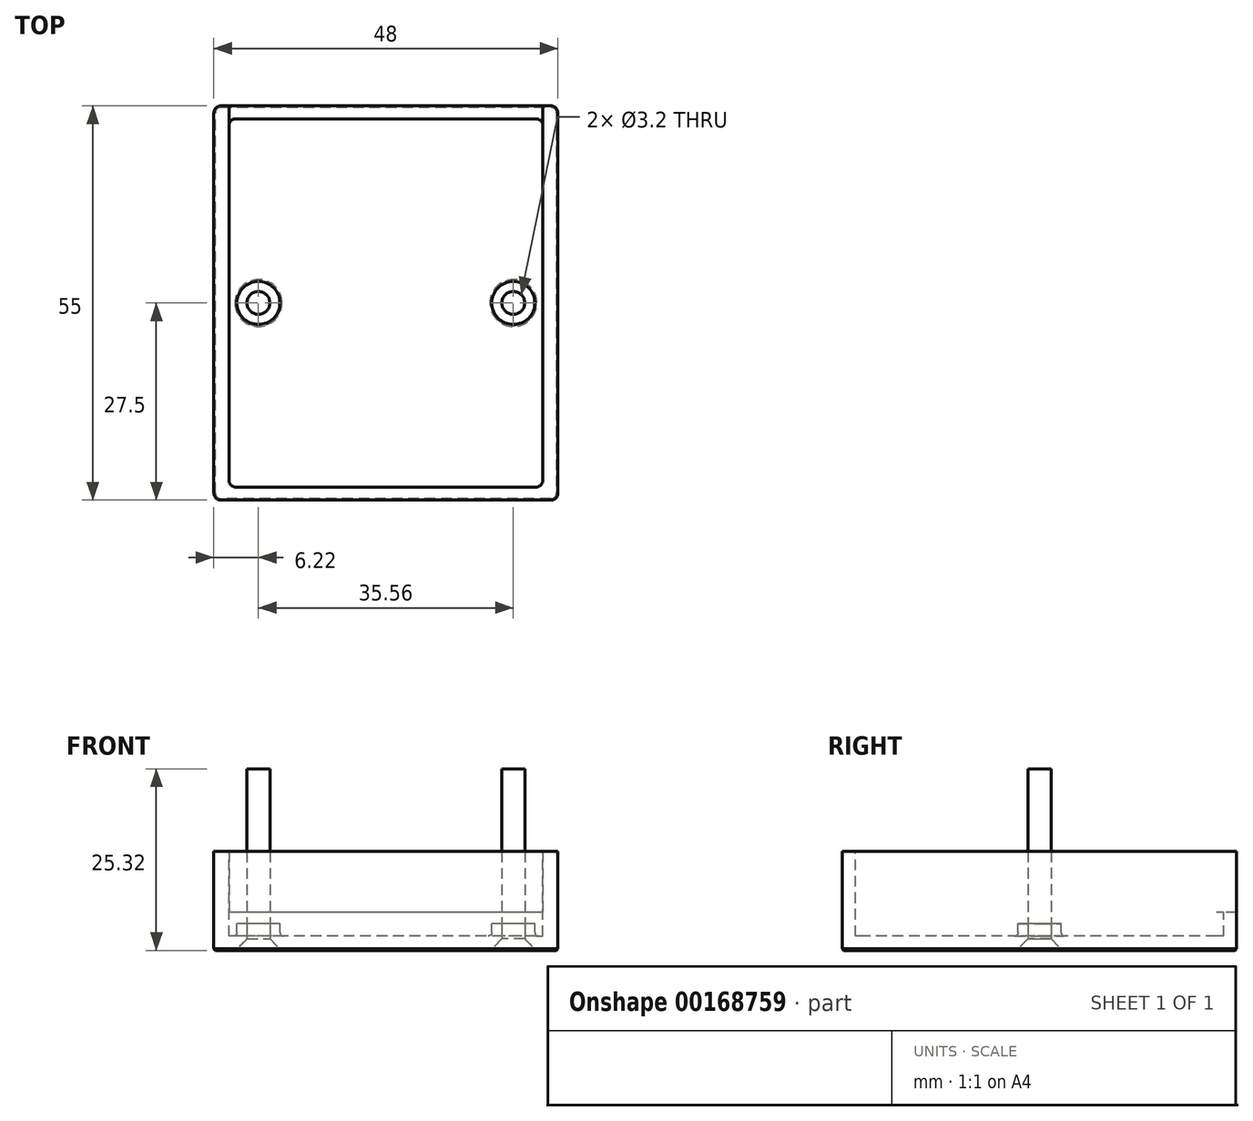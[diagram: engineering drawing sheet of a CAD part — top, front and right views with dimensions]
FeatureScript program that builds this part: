
annotation { "Feature Type Name" : "Feature", "Feature Type Description" : "" }
export const myFeature = defineFeature(function(context is Context, id is Id, definition is map)
    precondition{}
    {
        {
            var Q0;
            Q0=qCreatedBy(makeId("Top.planeOp"),FACE);
            var sketch = newSketch(context, id + "F0", { "sketchPlane" : qUnion([Q0])});
            skLineSegment(sketch, "E0.bottom", {"start": v(21.65, 25.45) * mm, "end": v(-21.65, 25.45) * mm, "construction": true});
            skLineSegment(sketch, "E0.top", {"start": v(21.65, -25.45) * mm, "end": v(-21.65, -25.45) * mm, "construction": true});
            skLineSegment(sketch, "E0.left", {"start": v(21.65, 25.45) * mm, "end": v(21.65, -25.45) * mm, "construction": true});
            skLineSegment(sketch, "E0.right", {"start": v(-21.65, 25.45) * mm, "end": v(-21.65, -25.45) * mm, "construction": true});
            skPoint(sketch, "E0.middle", {"position": v(0, 0) * mm});
            skLineSegment(sketch, "E1", {"start": v(-17.78, 0) * mm, "end": v(17.78, 0) * mm, "construction": true});
            skCircle(sketch, "E2", {"center": v(-17.78, 0) * mm, "radius": 1.6 * mm, "construction": true});
            skCircle(sketch, "E3", {"center": v(17.78, 0) * mm, "radius": 1.6 * mm, "construction": true});
            skSolve(sketch);
        }
        {
            var Q0;
            Q0=qCreatedBy(makeId("Front.planeOp"),FACE);
            var sketch = newSketch(context, id + "F1", { "sketchPlane" : qUnion([Q0])});
            skLineSegment(sketch, "E4.0", {"start": v(21.65, 0) * mm, "end": v(-21.65, 0) * mm, "construction": true});
            skLineSegment(sketch, "E5", {"start": v(0, 0) * mm, "end": v(0, 2) * mm});
            skLineSegment(sketch, "E6", {"start": v(0, 2) * mm, "end": v(0, 3.7) * mm});
            skLineSegment(sketch, "E7", {"start": v(0, 3.7) * mm, "end": v(0, 5.3) * mm});
            skLineSegment(sketch, "E8", {"start": v(0, 5.3) * mm, "end": v(0, 7.8) * mm});
            skLineSegment(sketch, "E9", {"start": v(0, 7.8) * mm, "end": v(0, 13.8) * mm});
            skSolve(sketch);
        }
        {
            var Q0;
            Q0=qCreatedBy(makeId("Front.planeOp"),FACE);
            var sketch = newSketch(context, id + "F2", { "sketchPlane" : qUnion([Q0])});
            skPoint(sketch, "E10.0", {"position": v(-17.78, 0) * mm});
            skPoint(sketch, "E11.0", {"position": v(17.78, 0) * mm});
            skLineSegment(sketch, "E12", {"start": v(-17.78, 0) * mm, "end": v(-17.78, 25.32) * mm});
            skLineSegment(sketch, "E13", {"start": v(-17.78, 25.32) * mm, "end": v(-19.38, 25.32) * mm});
            skLineSegment(sketch, "E14", {"start": v(-19.38, 25.32) * mm, "end": v(-19.38, 1.6) * mm});
            skLineSegment(sketch, "E15", {"start": v(-19.38, 1.6) * mm, "end": v(-20.98, 0) * mm});
            skLineSegment(sketch, "E16", {"start": v(-20.98, 0) * mm, "end": v(-17.78, 0) * mm});
            skSolve(sketch);
        }
        {
            var Q0;
            Q0=qCreatedBy(makeId("Top.planeOp"),FACE);
            var sketch = newSketch(context, id + "F3", { "sketchPlane" : qUnion([Q0])});
            skLineSegment(sketch, "E17.0", {"start": v(21.65, 25.45) * mm, "end": v(-21.65, 25.45) * mm, "construction": true});
            skLineSegment(sketch, "E18.0", {"start": v(-21.65, 25.45) * mm, "end": v(-21.65, -25.45) * mm, "construction": true});
            skLineSegment(sketch, "E19.0", {"start": v(21.65, -25.45) * mm, "end": v(-21.65, -25.45) * mm, "construction": true});
            skLineSegment(sketch, "E20.0", {"start": v(21.65, 25.45) * mm, "end": v(21.65, -25.45) * mm, "construction": true});
            skLineSegment(sketch, "E21.0", {"start": v(21.9, 25.7) * mm, "end": v(21.9, -25.7) * mm});
            skLineSegment(sketch, "E21.1", {"start": v(21.9, 25.7) * mm, "end": v(-21.9, 25.7) * mm});
            skLineSegment(sketch, "E21.2", {"start": v(-21.9, 25.7) * mm, "end": v(-21.9, -25.7) * mm});
            skLineSegment(sketch, "E21.3", {"start": v(21.9, -25.7) * mm, "end": v(-21.9, -25.7) * mm});
            skLineSegment(sketch, "E22.bottom", {"start": v(24, 27.5) * mm, "end": v(-24, 27.5) * mm});
            skLineSegment(sketch, "E22.top", {"start": v(24, -27.5) * mm, "end": v(-24, -27.5) * mm});
            skLineSegment(sketch, "E22.left", {"start": v(24, 27.5) * mm, "end": v(24, -27.5) * mm});
            skLineSegment(sketch, "E22.right", {"start": v(-24, 27.5) * mm, "end": v(-24, -27.5) * mm});
            skPoint(sketch, "E22.middle", {"position": v(0, 0) * mm});
            skCircle(sketch, "E23.0", {"center": v(-17.78, 0) * mm, "radius": 1.6 * mm, "construction": true});
            skCircle(sketch, "E24.0", {"center": v(17.78, 0) * mm, "radius": 1.6 * mm, "construction": true});
            skCircle(sketch, "E25", {"center": v(-17.78, 0) * mm, "radius": 3 * mm});
            skCircle(sketch, "E26", {"center": v(17.78, 0) * mm, "radius": 3 * mm});
            skSolve(sketch);
        }
        {
            var Q0;
            Q0=makeQuery(id+"F3.imprint","IMPRINT",FACE,{"disambiguationData":[TD([[makeQuery(id+"F3.imprint","IMPRINT",EDGE,{"derivedFrom":sQuery(id+"F3.wireOp",EDGE,"E23.0")}),1.0]])]});
            var Q1;
            Q1=makeQuery(id+"F3.imprint","IMPRINT",FACE,{"disambiguationData":[TD([[makeQuery(id+"F3.imprint","IMPRINT",EDGE,{"derivedFrom":sQuery(id+"F3.wireOp",EDGE,"E24.0")}),1.0]])]});
            var Q2;
            Q2=makeQuery(id+"F3.imprint","IMPRINT",FACE,{"disambiguationData":[TD([[makeQuery(id+"F3.imprint","IMPRINT",EDGE,{"derivedFrom":sQuery(id+"F3.wireOp",EDGE,"E21.0")}),-1.0]])]});
            var Q3;
            Q3=makeQuery(id+"F3.imprint","IMPRINT",FACE,{"disambiguationData":[TD([[makeQuery(id+"F3.imprint","IMPRINT",EDGE,{"derivedFrom":sQuery(id+"F3.wireOp",EDGE,"E25")}),1.0]])]});
            var Q4;
            Q4=makeQuery(id+"F3.imprint","IMPRINT",FACE,{"disambiguationData":[TD([[makeQuery(id+"F3.imprint","IMPRINT",EDGE,{"derivedFrom":sQuery(id+"F3.wireOp",EDGE,"E26")}),1.0]])]});
            var Q5;
            Q5=sQuery(id+"F1.wireOp",EDGE,"E5");
            sweep(context, id + "F4", {"profiles" : qUnion([Q0, Q1, Q2, Q3, Q4]), "path" : qUnion([Q5])});
        }
        {
            var Q0;
            Q0=makeQuery(id+"F3.imprint","IMPRINT",FACE,{"disambiguationData":[TD([[makeQuery(id+"F3.imprint","IMPRINT",EDGE,{"derivedFrom":sQuery(id+"F3.wireOp",EDGE,"E25")}),1.0]])]});
            var Q1;
            Q1=makeQuery(id+"F3.imprint","IMPRINT",FACE,{"disambiguationData":[TD([[makeQuery(id+"F3.imprint","IMPRINT",EDGE,{"derivedFrom":sQuery(id+"F3.wireOp",EDGE,"E26")}),1.0]])]});
            var Q2;
            Q2=sQuery(id+"F1.wireOp",EDGE,"E5");
            var Q3;
            Q3=sQuery(id+"F1.wireOp",EDGE,"E6");
            sweep(context, id + "F5", {"operationType" : NewBodyOperationType.ADD, "profiles" : qUnion([Q0, Q1]), "path" : qUnion([Q2, Q3])});
        }
        {
            var Q0;
            Q0=makeQuery(id+"F3.imprint","IMPRINT",FACE,{"disambiguationData":[TD([[makeQuery(id+"F3.imprint","IMPRINT",EDGE,{"derivedFrom":sQuery(id+"F3.wireOp",EDGE,"E21.0")}),1.0]])]});
            var Q1;
            Q1=sQuery(id+"F1.wireOp",EDGE,"E5");
            var Q2;
            Q2=sQuery(id+"F1.wireOp",EDGE,"E6");
            var Q3;
            Q3=sQuery(id+"F1.wireOp",EDGE,"E7");
            var Q4;
            Q4=sQuery(id+"F1.wireOp",EDGE,"E8");
            var Q5;
            Q5=sQuery(id+"F1.wireOp",EDGE,"E9");
            sweep(context, id + "F6", {"operationType" : NewBodyOperationType.ADD, "profiles" : qUnion([Q0]), "path" : qUnion([Q1, Q2, Q3, Q4, Q5])});
        }
        {
            var Q0;
            Q0=makeQuery(id+"F2.imprint","IMPRINT",FACE,{"disambiguationData":[TD([[makeQuery(id+"F2.imprint","IMPRINT",EDGE,{"derivedFrom":sQuery(id+"F2.wireOp",EDGE,"E12")}),1.0]])]});
            var Q1;
            Q1=sQuery(id+"F2.wireOp",EDGE,"E12");
            revolve(context, id + "F7", {"entities" : qUnion([Q0]), "axis" : qUnion([Q1]), "revolveType" : RevolveType.FULL});
        }
        {
            var Q0;
            Q0=makeQuery(id+"F7.opRevolve","SWEPT_BODY",BODY,{"disambiguationData":[OSD([sQuery(id+"F2.wireOp",EDGE,"E12"),sQuery(id+"F2.wireOp",EDGE,"E13"),sQuery(id+"F2.wireOp",EDGE,"E14"),sQuery(id+"F2.wireOp",EDGE,"E15"),sQuery(id+"F2.wireOp",EDGE,"E16")])]});
            var Q1;
            Q1=qCreatedBy(makeId("Right.planeOp"),FACE);
            mirror(context, id + "F8", {"entities" : qUnion([Q0]), "mirrorPlane" : qUnion([Q1])});
        }
        {
            var Q0;
            Q0=makeQuery(id+"F6.opSweep","CAP_FACE",FACE,{"disambiguationData":[OSD([sQuery(id+"F1.wireOp",VERTEX,"E9.end"),sQuery(id+"F3.wireOp",EDGE,"E21.0"),sQuery(id+"F3.wireOp",EDGE,"E21.1"),sQuery(id+"F3.wireOp",EDGE,"E21.2"),sQuery(id+"F3.wireOp",EDGE,"E21.3"),sQuery(id+"F3.wireOp",EDGE,"E22.bottom"),sQuery(id+"F3.wireOp",EDGE,"E22.top"),sQuery(id+"F3.wireOp",EDGE,"E22.left"),sQuery(id+"F3.wireOp",EDGE,"E22.right")])],"isStart":false});
            var sketch = newSketch(context, id + "F9", { "sketchPlane" : qUnion([Q0])});
            skLineSegment(sketch, "E27.0", {"start": v(-21.9, 25.7) * mm, "end": v(21.9, 25.7) * mm});
            skLineSegment(sketch, "E28.0", {"start": v(24, 27.5) * mm, "end": v(-24, 27.5) * mm, "construction": true});
            skLineSegment(sketch, "E29", {"start": v(-21.9, 25.7) * mm, "end": v(-21.9, 27.5) * mm});
            skLineSegment(sketch, "E30", {"start": v(-21.9, 27.5) * mm, "end": v(21.9, 27.5) * mm});
            skLineSegment(sketch, "E31", {"start": v(21.9, 27.5) * mm, "end": v(21.9, 25.7) * mm});
            skSolve(sketch);
        }
        {
            var Q0;
            Q0=makeQuery(id+"F9.imprint","IMPRINT",FACE,{"disambiguationData":[TD([[makeQuery(id+"F9.imprint","IMPRINT",EDGE,{"derivedFrom":sQuery(id+"F9.wireOp",EDGE,"E27.0")}),1.0]])]});
            var Q1;
            Q1=sQuery(id+"F1.wireOp",EDGE,"E9");
            var Q2;
            Q2=sQuery(id+"F1.wireOp",EDGE,"E8");
            sweep(context, id + "F13", {"operationType" : NewBodyOperationType.REMOVE, "profiles" : qUnion([Q0]), "path" : qUnion([Q1, Q2])});
        }
        {
            var Q0;
            Q0=makeQuery(id+"F8.opPattern","COPY",BODY,{"derivedFrom":makeQuery(id+"F7.opRevolve","SWEPT_BODY",BODY,{"disambiguationData":[OSD([sQuery(id+"F2.wireOp",EDGE,"E12"),sQuery(id+"F2.wireOp",EDGE,"E13"),sQuery(id+"F2.wireOp",EDGE,"E14"),sQuery(id+"F2.wireOp",EDGE,"E15"),sQuery(id+"F2.wireOp",EDGE,"E16")])]}),"instanceName":"1"});
            var Q1;
            Q1=makeQuery(id+"F7.opRevolve","SWEPT_BODY",BODY,{"disambiguationData":[OSD([sQuery(id+"F2.wireOp",EDGE,"E12"),sQuery(id+"F2.wireOp",EDGE,"E13"),sQuery(id+"F2.wireOp",EDGE,"E14"),sQuery(id+"F2.wireOp",EDGE,"E15"),sQuery(id+"F2.wireOp",EDGE,"E16")])]});
            var Q2;
            Q2=makeQuery(id+"F4.opSweep","SWEPT_BODY",BODY,{"disambiguationData":[OSD([sQuery(id+"F1.wireOp",EDGE,"E5"),sQuery(id+"F3.wireOp",EDGE,"E21.0"),sQuery(id+"F3.wireOp",EDGE,"E21.1"),sQuery(id+"F3.wireOp",EDGE,"E21.2"),sQuery(id+"F3.wireOp",EDGE,"E21.3")])]});
            booleanBodies(context, id + "F14", {"operationType" : BooleanOperationType.SUBTRACTION, "tools" : qUnion([Q0, Q1]), "targets" : qUnion([Q2]), "keepTools" : true});
        }
        {
            var Q0;
            Q0=makeQuery(id+"F6.opSweep","SWEPT_EDGE",EDGE,{"disambiguationData":[OSD([sQuery(id+"F1.wireOp",EDGE,"E5"),sQuery(id+"F3.wireOp",EDGE,"E21.0"),sQuery(id+"F3.wireOp",EDGE,"E21.3")])]});
            var Q1;
            Q1=makeQuery(id+"F6.opSweep","SWEPT_EDGE",EDGE,{"disambiguationData":[OSD([sQuery(id+"F1.wireOp",EDGE,"E5"),sQuery(id+"F3.wireOp",EDGE,"E21.0"),sQuery(id+"F3.wireOp",EDGE,"E21.1")])]});
            var Q2;
            Q2=makeQuery(id+"F6.opSweep","SWEPT_EDGE",EDGE,{"disambiguationData":[OSD([sQuery(id+"F1.wireOp",EDGE,"E5"),sQuery(id+"F3.wireOp",EDGE,"E21.2"),sQuery(id+"F3.wireOp",EDGE,"E21.3")])]});
            var Q3;
            Q3=makeQuery(id+"F6.opSweep","SWEPT_EDGE",EDGE,{"disambiguationData":[OSD([sQuery(id+"F1.wireOp",EDGE,"E5"),sQuery(id+"F3.wireOp",EDGE,"E21.1"),sQuery(id+"F3.wireOp",EDGE,"E21.2")])]});
            var Q4;
            Q4=makeQuery(id+"F6.opSweep","SWEPT_EDGE",EDGE,{"disambiguationData":[OSD([sQuery(id+"F1.wireOp",EDGE,"E9"),sQuery(id+"F3.wireOp",EDGE,"E22.bottom"),sQuery(id+"F3.wireOp",EDGE,"E22.right")])]});
            var Q5;
            Q5=makeQuery(id+"F6.opSweep","SWEPT_EDGE",EDGE,{"disambiguationData":[OSD([sQuery(id+"F1.wireOp",EDGE,"E9"),sQuery(id+"F3.wireOp",EDGE,"E22.bottom"),sQuery(id+"F3.wireOp",EDGE,"E22.left")])]});
            var Q6;
            Q6=makeQuery(id+"F6.opSweep","SWEPT_EDGE",EDGE,{"disambiguationData":[OSD([sQuery(id+"F1.wireOp",EDGE,"E9"),sQuery(id+"F3.wireOp",EDGE,"E22.top"),sQuery(id+"F3.wireOp",EDGE,"E22.right")])]});
            var Q7;
            Q7=makeQuery(id+"F6.opSweep","SWEPT_EDGE",EDGE,{"disambiguationData":[OSD([sQuery(id+"F1.wireOp",EDGE,"E9"),sQuery(id+"F3.wireOp",EDGE,"E22.top"),sQuery(id+"F3.wireOp",EDGE,"E22.left")])]});
            fillet(context, id + "F10", {"entities" : qUnion([Q0, Q1, Q2, Q3, Q4, Q5, Q6, Q7]), "radius" : 1 * mm, "allowEdgeOverflow" : false});
        }
        {
            var Q0;
            Q0=makeQuery(id+"F5.boolean.opBoolean","INTERSECT",EDGE,{"derivedFrom":[makeQuery(id+"F4.opSweep","CAP_FACE",FACE,{"disambiguationData":[OSD([sQuery(id+"F1.wireOp",VERTEX,"E5.end"),sQuery(id+"F3.wireOp",EDGE,"E21.0"),sQuery(id+"F3.wireOp",EDGE,"E21.1"),sQuery(id+"F3.wireOp",EDGE,"E21.2"),sQuery(id+"F3.wireOp",EDGE,"E21.3")])],"isStart":false}),makeQuery(id+"F5.opSweep","SWEPT_FACE",FACE,{"disambiguationData":[OSD([sQuery(id+"F1.wireOp",EDGE,"E5"),sQuery(id+"F3.wireOp",EDGE,"E25")])]})]});
            var Q1;
            Q1=makeQuery(id+"F5.boolean.opBoolean","INTERSECT",EDGE,{"derivedFrom":[makeQuery(id+"F4.opSweep","CAP_FACE",FACE,{"disambiguationData":[OSD([sQuery(id+"F1.wireOp",VERTEX,"E5.end"),sQuery(id+"F3.wireOp",EDGE,"E21.0"),sQuery(id+"F3.wireOp",EDGE,"E21.1"),sQuery(id+"F3.wireOp",EDGE,"E21.2"),sQuery(id+"F3.wireOp",EDGE,"E21.3")])],"isStart":false}),makeQuery(id+"F5.opSweep","SWEPT_FACE",FACE,{"disambiguationData":[OSD([sQuery(id+"F1.wireOp",EDGE,"E5"),sQuery(id+"F3.wireOp",EDGE,"E26")])]})]});
            var Q2;
            Q2=makeQuery(id+"F4.opSweep","CAP_EDGE",EDGE,{"disambiguationData":[OSD([sQuery(id+"F1.wireOp",VERTEX,"E5.end"),sQuery(id+"F3.wireOp",EDGE,"E21.1")])],"isStart":false});
            fillet(context, id + "F11", {"entities" : qUnion([Q0, Q1, Q2]), "radius" : 0.5 * mm, "tangentPropagation" : true, "allowEdgeOverflow" : false});
        }
        {
            var Q0;
            {var subQ0=sQuery(id+"F3.wireOp",EDGE,"E21.3");var subQ1=sQuery(id+"F3.wireOp",EDGE,"E21.2");var subQ2=sQuery(id+"F3.wireOp",EDGE,"E21.1");var subQ3=sQuery(id+"F3.wireOp",EDGE,"E21.0");var subQ4=sQuery(id+"F1.wireOp",VERTEX,"E5.start");Q0=makeQuery(id+"F6.boolean.opBoolean","MERGE",FACE,{"derivedFrom":[makeQuery(id+"F4.opSweep","CAP_FACE",FACE,{"disambiguationData":[OSD([subQ4,subQ3,subQ2,subQ1,subQ0])],"isStart":true}),makeQuery(id+"F6.opSweep","CAP_FACE",FACE,{"disambiguationData":[OSD([subQ4,subQ3,subQ2,subQ1,subQ0,sQuery(id+"F3.wireOp",EDGE,"E22.bottom"),sQuery(id+"F3.wireOp",EDGE,"E22.top"),sQuery(id+"F3.wireOp",EDGE,"E22.left"),sQuery(id+"F3.wireOp",EDGE,"E22.right")])],"isStart":true})]});}
            chamfer(context, id + "F12", {"entities" : qUnion([Q0]), "width" : 0.2 * mm});
        }
    });
